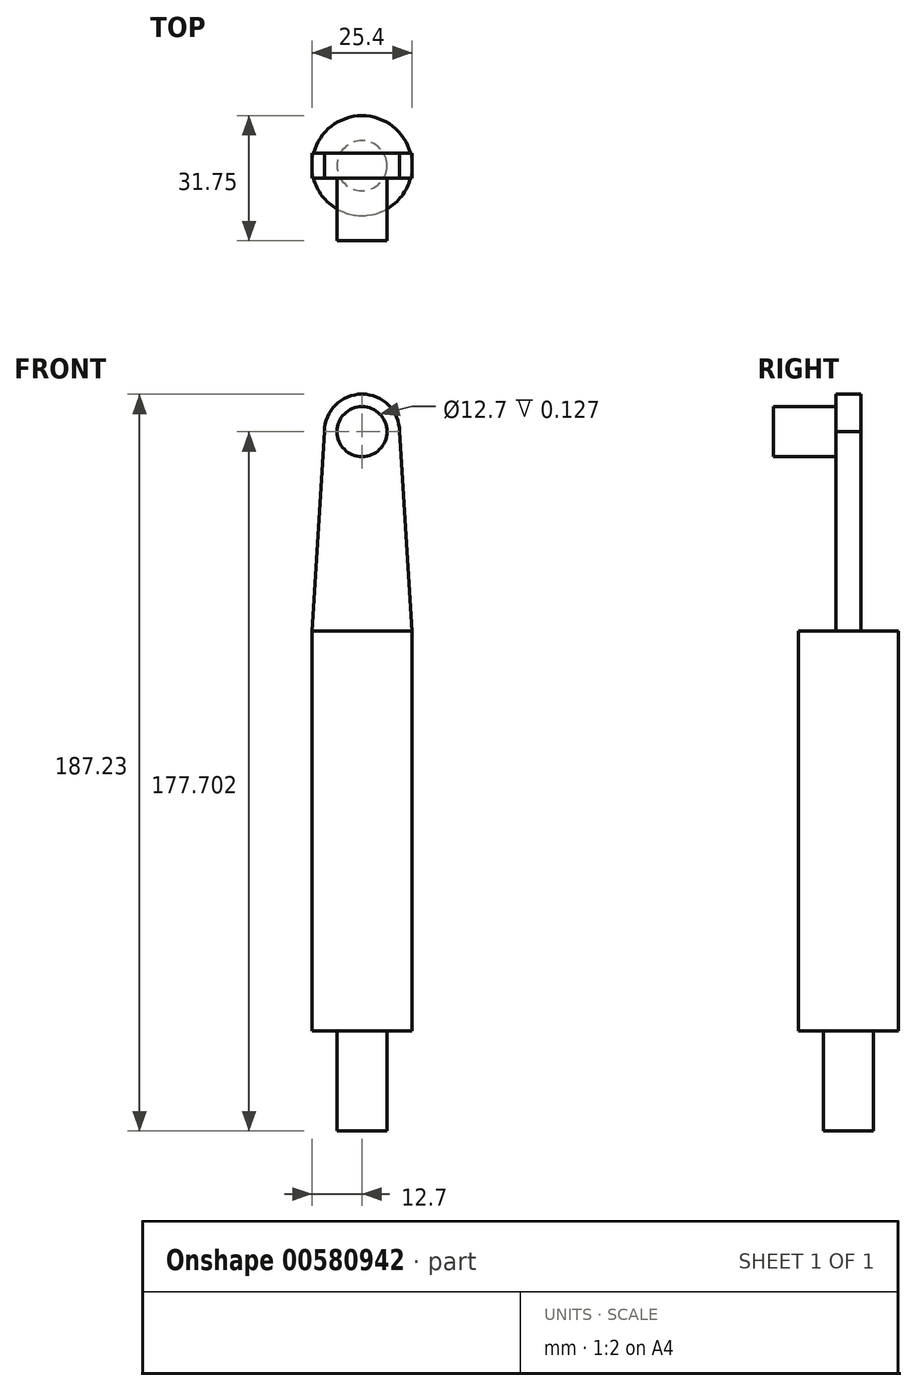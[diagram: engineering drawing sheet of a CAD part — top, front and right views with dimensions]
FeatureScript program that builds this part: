
annotation { "Feature Type Name" : "Feature", "Feature Type Description" : "" }
export const myFeature = defineFeature(function(context is Context, id is Id, definition is map)
    precondition{}
    {
        {
            var Q0;
            Q0=qCreatedBy(makeId("Front.planeOp"),FACE);
            var sketch = newSketch(context, id + "F0", { "sketchPlane" : qUnion([Q0])});
            skLineSegment(sketch, "E0.bottom", {"start": v(-12.7, 93.7) * mm, "end": v(12.7, 93.7) * mm});
            skLineSegment(sketch, "E0.top", {"start": v(-12.7, -7.9) * mm, "end": v(12.7, -7.9) * mm});
            skLineSegment(sketch, "E0.left", {"start": v(-12.7, 93.7) * mm, "end": v(-12.7, -7.9) * mm});
            skLineSegment(sketch, "E0.right", {"start": v(12.7, 93.7) * mm, "end": v(12.7, -7.9) * mm});
            skCircle(sketch, "E1", {"center": v(0, 144.4) * mm, "radius": 9.53 * mm});
            skLineSegment(sketch, "E2", {"start": v(-12.7, 93.7) * mm, "end": v(-9.52, 144.4) * mm});
            skLineSegment(sketch, "E3", {"start": v(12.7, 93.7) * mm, "end": v(9.53, 144.4) * mm});
            skCircle(sketch, "E4", {"center": v(0, 144.4) * mm, "radius": 6.35 * mm});
            skLineSegment(sketch, "E5", {"start": v(0, 93.7) * mm, "end": v(0, -7.9) * mm});
            skLineSegment(sketch, "E6", {"start": v(0, -7.9) * mm, "end": v(0, -33.3) * mm});
            skLineSegment(sketch, "E7", {"start": v(0, -33.3) * mm, "end": v(6.35, -33.3) * mm});
            skLineSegment(sketch, "E8", {"start": v(0, -33.3) * mm, "end": v(-6.35, -33.3) * mm});
            skLineSegment(sketch, "E9", {"start": v(6.35, -33.3) * mm, "end": v(6.35, -7.9) * mm});
            skLineSegment(sketch, "E10", {"start": v(-6.35, -33.3) * mm, "end": v(-6.35, -7.9) * mm});
            skSolve(sketch);
        }
        {
            var Q0;
            {var subQ0=sQuery(id+"F0.wireOp",EDGE,"E0.right");Q0=makeQuery(id+"F0.imprint","IMPRINT",FACE,{"disambiguationData":[TD([[makeQuery(id+"F0.imprint","IMPRINT",EDGE,{"derivedFrom":subQ0}),-1.0]])]});}
            var Q1;
            Q1=sQuery(id+"F0.wireOp",EDGE,"E5");
            revolve(context, id + "F1", {"entities" : qUnion([Q0]), "axis" : qUnion([Q1]), "revolveType" : RevolveType.FULL});
        }
        {
            var Q0;
            {var subQ0=sQuery(id+"F0.wireOp",EDGE,"E2");Q0=makeQuery(id+"F0.imprint","IMPRINT",FACE,{"disambiguationData":[TD([[makeQuery(id+"F0.imprint","IMPRINT",EDGE,{"derivedFrom":subQ0}),-1.0]])]});}
            extrude(context, id + "F2", {"entities" : qUnion([Q0]), "operationType" : NewBodyOperationType.ADD, "endBound" : BoundingType.SYMMETRIC, "depth" : 6.35 * mm, "offsetDistance" : 25.4 * mm});
        }
        {
            var Q0;
            Q0=makeQuery(id+"F0.imprint","IMPRINT",FACE,{"disambiguationData":[TD([[makeQuery(id+"F0.imprint","IMPRINT",EDGE,{"derivedFrom":sQuery(id+"F0.wireOp",EDGE,"E4")}),-1.0]])]});
            extrude(context, id + "F3", {"entities" : qUnion([Q0]), "operationType" : NewBodyOperationType.ADD, "endBound" : BoundingType.SYMMETRIC, "depth" : 6.35 * mm, "offsetDistance" : 25.4 * mm});
        }
        {
            var Q0;
            Q0=makeQuery(id+"F0.imprint","IMPRINT",FACE,{"disambiguationData":[TD([[makeQuery(id+"F0.imprint","IMPRINT",EDGE,{"derivedFrom":sQuery(id+"F0.wireOp",EDGE,"E4")}),1.0]])]});
            extrude(context, id + "F4", {"entities" : qUnion([Q0]), "operationType" : NewBodyOperationType.ADD, "depth" : 19.05 * mm, "offsetDistance" : 25.4 * mm});
        }
        {
            var Q0;
            {var subQ0=sQuery(id+"F0.wireOp",EDGE,"E6");Q0=makeQuery(id+"F0.imprint","IMPRINT",FACE,{"disambiguationData":[TD([[makeQuery(id+"F0.imprint","IMPRINT",EDGE,{"derivedFrom":subQ0}),1.0]])]});}
            var Q1;
            Q1=sQuery(id+"F0.wireOp",EDGE,"E6");
            revolve(context, id + "F5", {"operationType" : NewBodyOperationType.ADD, "entities" : qUnion([Q0]), "axis" : qUnion([Q1]), "revolveType" : RevolveType.FULL});
        }
        {
            var Q0;
            Q0=makeQuery(id+"F0.imprint","IMPRINT",FACE,{"disambiguationData":[TD([[makeQuery(id+"F0.imprint","IMPRINT",EDGE,{"derivedFrom":sQuery(id+"F0.wireOp",EDGE,"E4")}),1.0]])]});
            extrude(context, id + "F6", {"entities" : qUnion([Q0]), "operationType" : NewBodyOperationType.ADD, "oppositeDirection" : true, "depth" : 3.05 * mm, "offsetDistance" : 25.4 * mm});
        }
    });
